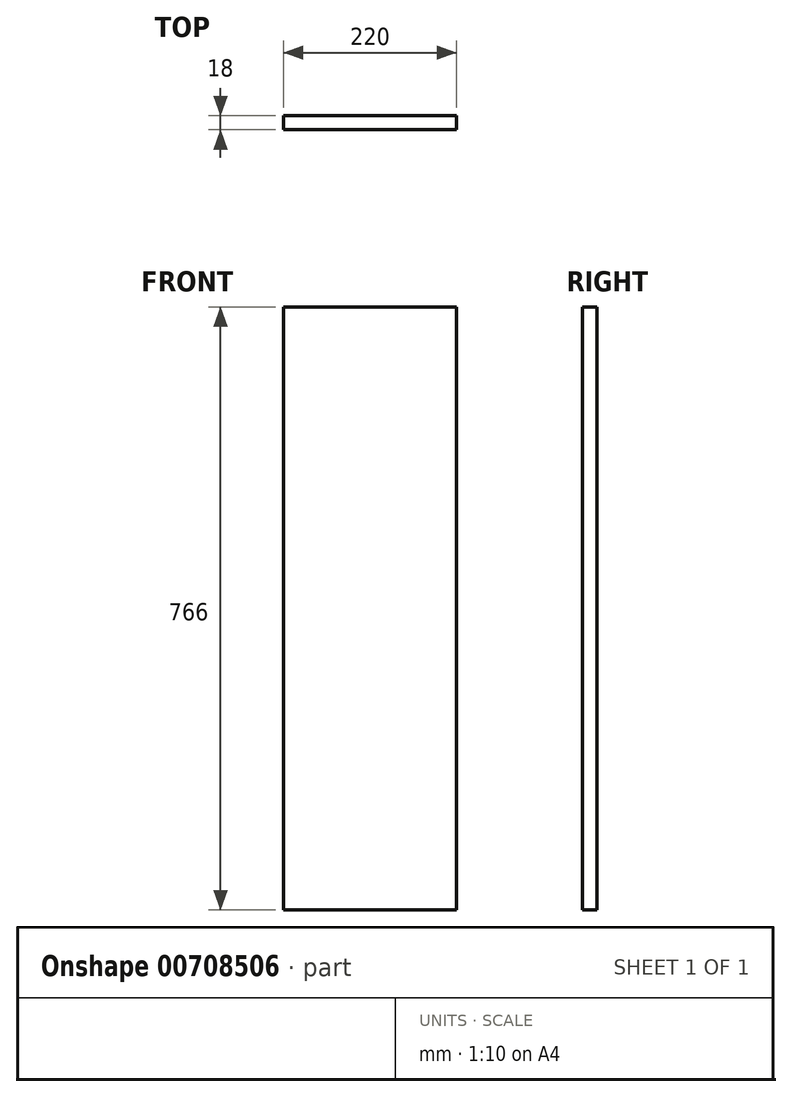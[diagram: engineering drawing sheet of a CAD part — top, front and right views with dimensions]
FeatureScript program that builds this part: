
annotation { "Feature Type Name" : "Feature", "Feature Type Description" : "" }
export const myFeature = defineFeature(function(context is Context, id is Id, definition is map)
    precondition{}
    {
        {
            var Q0;
            Q0=qCreatedBy(makeId("Front.planeOp"),FACE);
            var sketch = newSketch(context, id + "F0", { "sketchPlane" : qUnion([Q0])});
            skLineSegment(sketch, "E0.bottom", {"start": v(0, 0) * mm, "end": v(-220, 0) * mm});
            skLineSegment(sketch, "E0.top", {"start": v(0, -766) * mm, "end": v(-220, -766) * mm});
            skLineSegment(sketch, "E0.left", {"start": v(0, 0) * mm, "end": v(0, -766) * mm});
            skLineSegment(sketch, "E0.right", {"start": v(-220, 0) * mm, "end": v(-220, -766) * mm});
            skSolve(sketch);
        }
        {
            var Q0;
            Q0=qSketchRegion(id+"F0",true);
            extrude(context, id + "F1", {"entities" : qUnion([Q0]), "depth" : 18 * mm, "offsetDistance" : 25 * mm});
        }
    });
